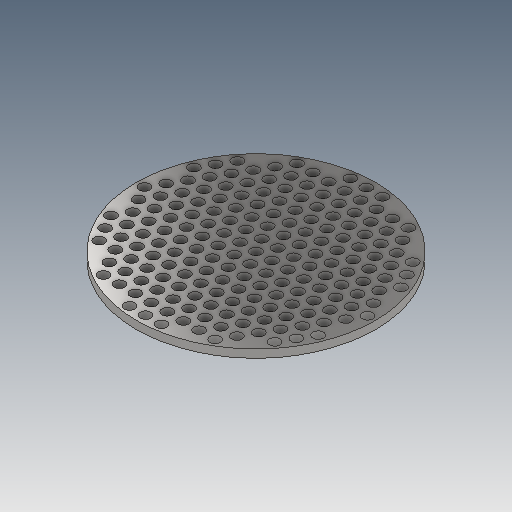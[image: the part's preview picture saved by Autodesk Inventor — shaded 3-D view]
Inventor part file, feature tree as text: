
AUTODESK INVENTOR PART (.ipt)
format: ipt  version: 2025 (Build 290162000, 162)  size: 684,544 bytes
history: native  units: mm
features: extrude x1, sketch x1
ambient origin geometry x8: Origin, YZ Plane, XZ Plane, XY Plane, X Axis, Y Axis, Z Axis, Center Point
bodies: Body1 (feature_tree)
feature tree (2):
  extrude  "拉伸2"  Depth=1.5mm
  sketch  "草图2"  dims[d27=2.0mm d28=2.0mm d29=2.0mm d30=2.0mm d31=2.0mm d32=2.0mm d33=2.0mm d34=2.0mm d35=2.0mm d36=2.0mm d37=2.0mm d38=2.0mm d39=2.0mm d42=2.0mm d44=2.0mm d45=2.0mm d46=2.0mm d47=2.0mm d48=2.0mm d49=2.0mm d50=2.0mm d51=2.0mm d55=2.0mm d56=2.0mm d57=2.0mm d58=2.0mm d59=2.0mm d60=2.0mm d61=2.0mm d62=2.0mm d63=2.0mm d64=2.0mm d65=2.0mm d66=2.0mm d67=2.0mm d68=2.0mm d69=2.0mm d70=2.0mm d71=2.0mm d72=2.0mm d73=2.0mm d74=2.0mm d75=2.0mm d76=2.0mm d77=2.0mm d78=2.0mm d79=2.0mm d82=2.0mm d83=2.0mm d84=2.0mm d85=2.0mm d86=2.0mm d87=2.0mm d89=2.0mm d91=2.0mm d92=2.0mm d94=2.0mm d95=2.0mm d96=2.0mm d97=2.0mm d98=2.0mm d99=2.0mm d100=2.0mm d101=2.0mm d102=2.0mm d103=2.0mm d104=2.0mm d105=2.0mm d106=2.0mm d107=2.0mm d109=2.0mm d110=2.0mm d111=2.0mm d113=2.0mm d114=2.0mm d116=2.0mm d117=2.0mm d118=2.0mm d119=2.0mm d120=2.0mm d121=2.0mm d122=2.0mm d123=2.0mm d124=2.0mm d125=2.0mm d126=2.0mm d127=2.0mm d128=2.0mm d129=2.0mm d130=2.0mm d131=2.0mm d132=2.0mm d133=2.0mm d134=2.0mm d135=2.0mm d136=2.0mm d137=2.0mm d138=2.0mm d139=2.0mm d140=2.0mm d141=2.0mm d142=45.0mm d143=1.5mm d144=0.0mm d3=0.5mm d4=0.872665mm d5=0.5mm d6=0.872665mm]
